# Revit family: Electrical_Equipment-Floor_Box-Hubbell_Wiring-Utility_Box-HBLSCCUBPDW
name_source: partatom
category: Electrical Fixtures
revit_build: Autodesk Revit 2015 (Build: 20140606_1530(x64)
units: mm (PartAtom-declared; Revit-internal decimal feet)

## types (2) — shared parameters
Apparent Load = 0 VA
Cover Material = Metal - Hubbell - Aluminum
Default Elevation = 0.000"
Load Classification = Other
Manufacturer = Hubbell-Wiring
Product Documentation Link = http://www.hubbell-wiring.com
Product Page URL = http://ecatalog.hubbell-wiring.com
Product data url = https://bimobject.com
URL = http://www.hubbell-wiring.com
Voltage = 0 V

## per-type parameters (varying)
| type | Box Material | Description | Model |
| Painted Galvanized Steel Box | Metal - Hubbell - Green Finish | Convention Center Utility Box, Painted Galvanized Steel | HBLSCCUBPDW |
| Stainless Steel Box | Metal - Hubbell - Steel | Convention Center Utility Box, Stainless Steel | HBLSCCUBPDWSS |

## geometry (parser evidence)
native form markers: Blend x6, Sweep x3
no freeform markers — native parametric forms only
